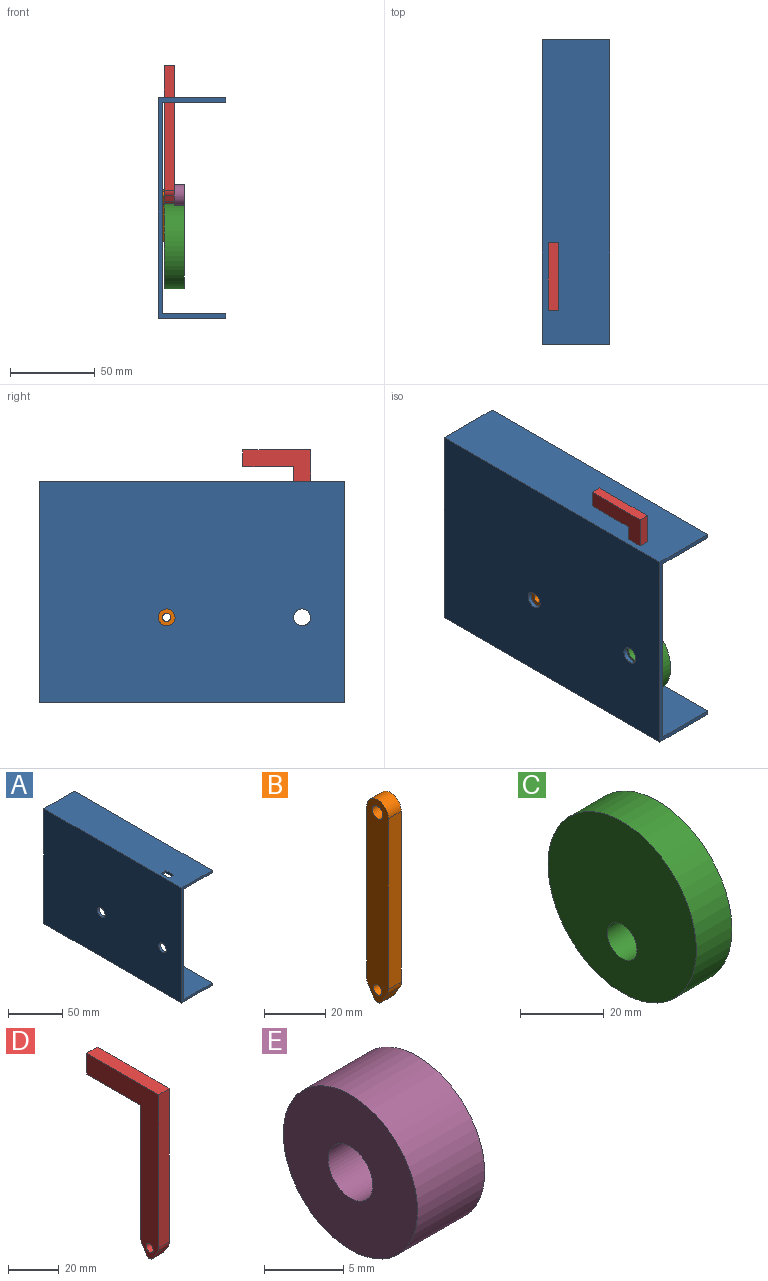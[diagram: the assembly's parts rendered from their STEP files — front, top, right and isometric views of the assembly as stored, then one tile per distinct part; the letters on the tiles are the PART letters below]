
ASSEMBLY  parts=5 mates=6
PART A: 16 faces, bbox 40x180x130 mm
  f0: plane 180x2.5mm, normal (1,0,0), area 450mm2, adj f1,f3,f4,f8
  f1: plane 130x40mm, normal (0,-1,0), area 512.5mm2, adj f0,f2,f4,f5,f6,f7,f8,f9
  f2: plane 180x40mm, normal (0,0,-1), area 7200mm2, adj f1,f3,f5,f6
  f3: plane 130x40mm, normal (0,1,0), area 512.5mm2, adj f0,f2,f4,f5,f6,f7,f8,f9
  f4: plane 180x40mm, normal (0,0,1), area 7140mm2, adj f0,f1,f3,f6,f12,f13,f14,f15
  f5: plane 180x2.5mm, normal (1,0,0), area 450mm2, adj f1,f2,f3,f7
  f6: plane 180x130mm, normal (-1,0,0), area 23242.9mm2, adj f1,f2,f3,f4,f10,f11
  f7: plane 180x37.5mm, normal (0,0,1), area 6750mm2, adj f1,f3,f5,f9
  f8: plane 180x37.5mm, normal (0,0,-1), area 6690mm2, adj f0,f1,f3,f9,f12,f13,f14,f15
  f9: plane 180x125mm, normal (1,0,0), area 22342.9mm2, adj f1,f3,f7,f8,f10,f11
  f10: cylinder r=5mm len=10mm, axis (1,0,0), area 78.5mm2, adj f6,f9
  f11: cylinder r=5mm len=10mm, axis (1,0,0), area 78.5mm2, adj f6,f9
  f12: plane 10x2.5mm, normal (1,0,0), area 25mm2, adj f4,f8,f13,f14
  f13: plane 6x2.5mm, normal (0,-1,0), area 15mm2, adj f4,f8,f12,f15
  f14: plane 6x2.5mm, normal (0,1,0), area 15mm2, adj f4,f8,f12,f15
  f15: plane 10x2.5mm, normal (-1,0,0), area 25mm2, adj f4,f8,f13,f14
PART B: 13 faces, bbox 6x10x81.2 mm
  f0: plane 81.23x10mm, normal (-1,0,0), area 744.3mm2, adj f1,f3,f4,f5,f6,f7,f8,f9
  f1: plane 68.57x6mm, normal (0,-1,0), area 411.4mm2, adj f0,f2,f9,f11
  f2: plane 81.23x10mm, normal (1,0,0), area 744.3mm2, adj f1,f3,f4,f5,f6,f7,f8,f9
  f3: plane 68.57x6mm, normal (0,1,0), area 411.4mm2, adj f0,f2,f9,f12
  f4: plane 6x4.07mm, normal (0,-0.85,-0.53), area 28.8mm2, adj f0,f2,f6,f11
  f5: plane 6x4.07mm, normal (0,0.85,-0.53), area 28.8mm2, adj f0,f2,f6,f12
  f6: cylinder r=2mm len=6mm, axis (1,0,0), area 24.3mm2, adj f0,f2,f4,f5
  f7: cylinder r=0.07mm len=6mm, axis (1,0,0), area 2.8mm2, adj f0,f2
  f8: cylinder r=2mm len=6mm, axis (1,0,0), area 75.4mm2, adj f0,f2
  f9: cylinder r=5mm len=10mm, axis (1,0,0), area 94.2mm2, adj f0,f1,f2,f3
  f10: cylinder r=2.5mm len=6mm, axis (1,0,0), area 94.2mm2, adj f0,f2
  f11: cylinder r=5mm len=6mm, axis (1,0,0), area 16.8mm2, adj f0,f1,f2,f4
  f12: cylinder r=5mm len=6mm, axis (-1,0,0), area 16.8mm2, adj f0,f2,f3,f5
PART C: 4 faces, bbox 12x50x50 mm
  f0: cylinder r=25mm len=50mm, axis (-1,0,0), area 1885mm2, adj f1,f2
  f1: plane 50x50mm, normal (1,0,0), area 1885mm2, adj f0,f3
  f2: plane 50x50mm, normal (-1,0,0), area 1885mm2, adj f0,f3
  f3: cylinder r=5mm len=12mm, axis (1,0,0), area 377mm2, adj f1,f2
PART D: 13 faces, bbox 6x40x81.2 mm
  f0: plane 81.23x40mm, normal (-1,0,0), area 1074.7mm2, adj f1,f3,f4,f5,f6,f7,f8,f9
  f1: plane 73.57x6mm, normal (0,-1,0), area 441.4mm2, adj f0,f2,f4,f11
  f2: plane 81.23x40mm, normal (1,0,0), area 1074.7mm2, adj f1,f3,f4,f5,f6,f7,f8,f9
  f3: plane 63.57x6mm, normal (0,1,0), area 381.4mm2, adj f0,f2,f9,f12
  f4: plane 40x6mm, normal (0,0,1), area 240mm2, adj f0,f1,f2,f10
  f5: plane 6x4.07mm, normal (0,-0.85,-0.53), area 28.8mm2, adj f0,f2,f7,f11
  f6: plane 6x4.07mm, normal (0,0.85,-0.53), area 28.8mm2, adj f0,f2,f7,f12
  f7: cylinder r=2mm len=6mm, axis (1,0,0), area 24.3mm2, adj f0,f2,f5,f6
  f8: cylinder r=2mm len=6mm, axis (1,0,0), area 75.4mm2, adj f0,f2
  f9: plane 30x6mm, normal (0,0,-1), area 180mm2, adj f0,f2,f3,f10
  f10: plane 10x6mm, normal (0,1,0), area 60mm2, adj f0,f2,f4,f9
  f11: cylinder r=5mm len=6mm, axis (1,0,0), area 16.8mm2, adj f0,f1,f2,f5
  f12: cylinder r=5mm len=6mm, axis (-1,0,0), area 16.8mm2, adj f0,f2,f3,f6
PART E: 4 faces, bbox 6x12x12 mm
  f0: cylinder r=6mm len=12mm, axis (-1,0,0), area 226.2mm2, adj f1,f2
  f1: plane 12x12mm, normal (1,0,0), area 100.5mm2, adj f0,f3
  f2: plane 12x12mm, normal (-1,0,0), area 100.5mm2, adj f0,f3
  f3: cylinder r=2mm len=6mm, axis (1,0,0), area 75.4mm2, adj f1,f2
PLACE A at identity fixed
PLACE B rot(axis=(-1,0,0),108deg) t=(2.5,30.44,79.43)mm
PLACE C rot(axis=(-1,0,0),140.1deg) t=(9.5,31.41,42.33)mm
PLACE D t=(3.5,20,63.88)mm
PLACE E rot(axis=(1,0,0),163.4deg) t=(12.5,25,72.66)mm
MATE planar D.f2 <-> A.f15  axis (1,0,0) through (9.5,30.58,119.52)mm
MATE cylindrical C.f3 <-> A.f11  axis (1,0,0) through (3.5,25,50)mm
MATE planar C.f0 <-> A.f11  axis (-1,0,0) through (3.5,31.41,42.33)mm
MATE revolute E.f3 <-> D.f8  axis (1,0,0) through (9.5,25,72.66)mm
MATE revolute B.f9 <-> A.f10  axis (1,0,0) through (2.5,105,50)mm
MATE planar D.f1 <-> A.f14  axis (0,-1,0) through (6.5,20,112.1)mm
